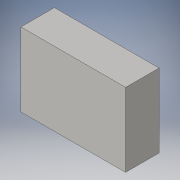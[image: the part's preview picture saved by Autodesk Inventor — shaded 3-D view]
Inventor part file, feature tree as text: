
AUTODESK INVENTOR PART (.ipt)
format: ipt  version: 2016 (Build 200138000, 138)  size: 82,432 bytes
history: native  units: in
note: dims shown in document units (in); Inventor stores cm internally (conversion verified against a paired STEP export)
features: extrude x1, sketch x1
ambient origin geometry x8: Origin, YZ Plane, XZ Plane, XY Plane, X Axis, Y Axis, Z Axis, Center Point
bodies: Solid1 (feature_tree)
feature tree (2):
  extrude  "Extrusion1"  Depth=3.126in
  sketch  "Sketch1"  dims[d0=2.2in d1=3.126in d2=1.0in d3=0.0in]
